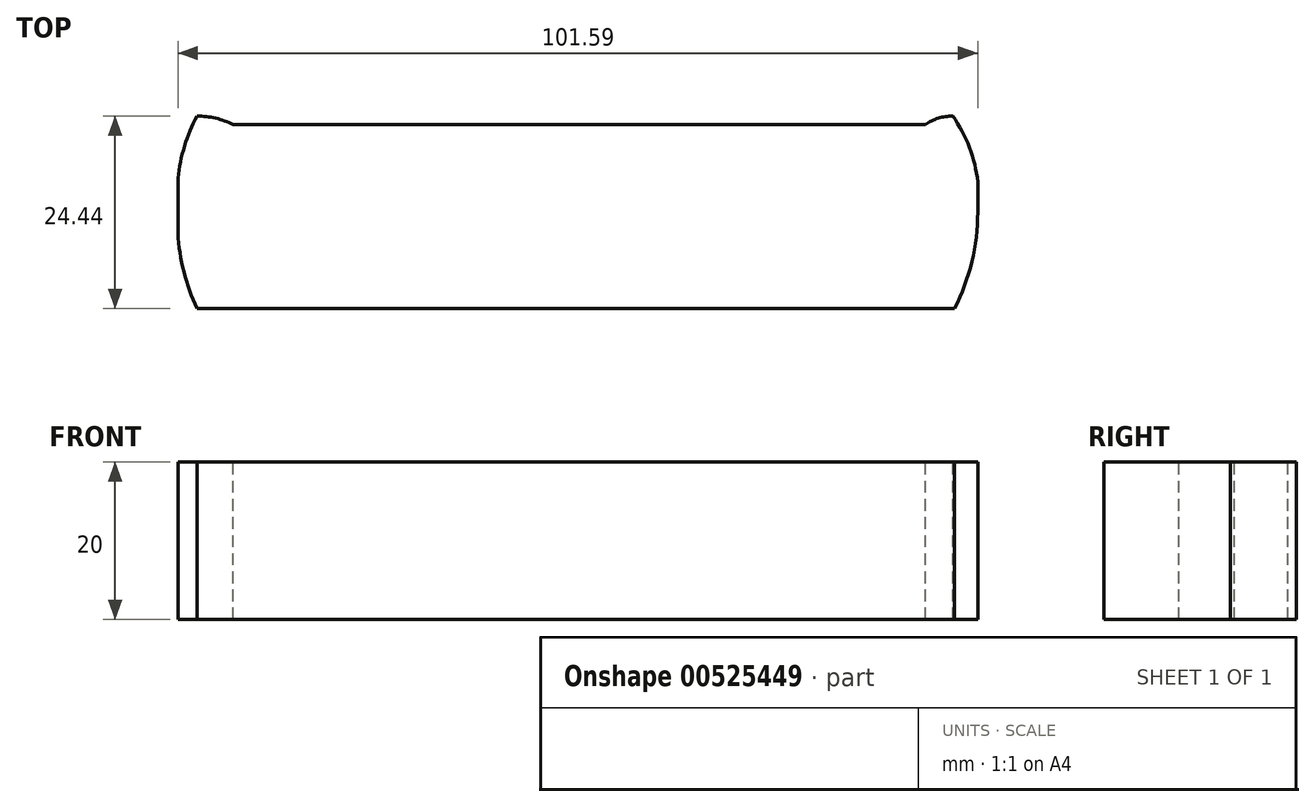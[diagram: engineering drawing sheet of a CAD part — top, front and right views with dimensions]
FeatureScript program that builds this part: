
annotation { "Feature Type Name" : "Feature", "Feature Type Description" : "" }
export const myFeature = defineFeature(function(context is Context, id is Id, definition is map)
    precondition{}
    {
        {
            var Q0;
            Q0=qCreatedBy(makeId("Top.planeOp"),FACE);
            var sketch = newSketch(context, id + "F0", { "sketchPlane" : qUnion([Q0])});
            skLineSegment(sketch, "E0.bottom", {"start": v(-50.41, 24.44) * mm, "end": v(51.18, 24.44) * mm});
            skLineSegment(sketch, "E0.top", {"start": v(-50.41, 0) * mm, "end": v(51.18, 0) * mm});
            skLineSegment(sketch, "E0.left", {"start": v(-50.41, 24.44) * mm, "end": v(-50.41, 0) * mm});
            skLineSegment(sketch, "E0.right", {"start": v(51.18, 24.44) * mm, "end": v(51.18, 0) * mm});
            skSolve(sketch);
        }
        {
            var Q0;
            Q0 = qSketchRegion(id + "F0", true);
            extrude(context, id + "F1", {"entities" : qUnion([Q0]), "depth" : 20 * mm, "offsetDistance" : 25 * mm});
        }
        {
            var Q0;
            Q0=makeQuery(id+"F1.opExtrude","CAP_FACE",FACE,{"disambiguationData":[OSD([sQuery(id+"F0.wireOp",EDGE,"E0.bottom"),sQuery(id+"F0.wireOp",EDGE,"E0.top"),sQuery(id+"F0.wireOp",EDGE,"E0.left"),sQuery(id+"F0.wireOp",EDGE,"E0.right")])],"isStart":false});
            var sketch = newSketch(context, id + "F2", { "sketchPlane" : qUnion([Q0])});
            skArc(sketch, "E1", {"start": v(-48, 24.44) * mm, "mid": v(-50.12, 18.51) * mm, "end": v(-50.41, 12.22) * mm});
            skArc(sketch, "E2", {"start": v(-50.41, 12.22) * mm, "mid": v(-49.97, 5.96) * mm, "end": v(-48, 0) * mm});
            skArc(sketch, "E3", {"start": v(51.18, 12.22) * mm, "mid": v(50.7, 18.62) * mm, "end": v(48, 24.44) * mm});
            skArc(sketch, "E4", {"start": v(48.22, 0) * mm, "mid": v(50.43, 5.93) * mm, "end": v(51.18, 12.22) * mm});
            skSolve(sketch);
        }
        {
            var Q0;
            {var subQ0=sQuery(id+"F2.wireOp",EDGE,"E1");var subQ1=makeQuery(id+"F1.opExtrude","CAP_EDGE",EDGE,{"disambiguationData":[OSD([sQuery(id+"F0.wireOp",EDGE,"E0.bottom")])],"isStart":false});var subQ2=makeQuery(id+"F2.imprint","INTERSECT",VERTEX,{"derivedFrom":[subQ1,subQ0]});Q0=makeQuery(id+"F2.imprint","IMPRINT",FACE,{"disambiguationData":[TD([[makeQuery(id+"F2.imprint","IMPRINT",EDGE,{"disambiguationData":[TD([[subQ2,-1.0]])],"derivedFrom":subQ0}),-1.0]])]});}
            var Q1;
            {var subQ0=sQuery(id+"F2.wireOp",EDGE,"E2");var subQ1=makeQuery(id+"F1.opExtrude","CAP_EDGE",EDGE,{"disambiguationData":[OSD([sQuery(id+"F0.wireOp",EDGE,"E0.top")])],"isStart":false});var subQ2=makeQuery(id+"F2.imprint","INTERSECT",VERTEX,{"derivedFrom":[subQ1,subQ0]});Q1=makeQuery(id+"F2.imprint","IMPRINT",FACE,{"disambiguationData":[TD([[makeQuery(id+"F2.imprint","IMPRINT",EDGE,{"disambiguationData":[TD([[subQ2,1.0]])],"derivedFrom":subQ0}),-1.0]])]});}
            var Q2;
            {var subQ0=sQuery(id+"F2.wireOp",EDGE,"E3");var subQ1=makeQuery(id+"F1.opExtrude","CAP_EDGE",EDGE,{"disambiguationData":[OSD([sQuery(id+"F0.wireOp",EDGE,"E0.bottom")])],"isStart":false});var subQ2=makeQuery(id+"F2.imprint","INTERSECT",VERTEX,{"derivedFrom":[subQ1,subQ0]});Q2=makeQuery(id+"F2.imprint","IMPRINT",FACE,{"disambiguationData":[TD([[makeQuery(id+"F2.imprint","IMPRINT",EDGE,{"disambiguationData":[TD([[subQ2,1.0]])],"derivedFrom":subQ0}),-1.0]])]});}
            var Q3;
            {var subQ0=sQuery(id+"F2.wireOp",EDGE,"E4");Q3=makeQuery(id+"F2.imprint","IMPRINT",FACE,{"disambiguationData":[TD([[makeQuery(id+"F2.imprint","IMPRINT",EDGE,{"derivedFrom":subQ0}),-1.0]])]});}
            extrude(context, id + "F3", {"entities" : qUnion([Q0, Q1, Q2, Q3]), "operationType" : NewBodyOperationType.REMOVE, "oppositeDirection" : true, "depth" : 25 * mm, "offsetDistance" : 25 * mm});
        }
        {
            var Q0;
            Q0=makeQuery(id+"F1.opExtrude","CAP_FACE",FACE,{"disambiguationData":[OSD([sQuery(id+"F0.wireOp",EDGE,"E0.bottom"),sQuery(id+"F0.wireOp",EDGE,"E0.top"),sQuery(id+"F0.wireOp",EDGE,"E0.left"),sQuery(id+"F0.wireOp",EDGE,"E0.right")])],"isStart":false});
            var sketch = newSketch(context, id + "F4", { "sketchPlane" : qUnion([Q0])});
            skArc(sketch, "E5", {"start": v(-43.4, 23.37) * mm, "mid": v(-45.64, 24.17) * mm, "end": v(-48, 24.44) * mm});
            skArc(sketch, "E6", {"start": v(48, 24.44) * mm, "mid": v(46.17, 24.17) * mm, "end": v(44.5, 23.37) * mm});
            skLineSegment(sketch, "E7", {"start": v(44.5, 23.37) * mm, "end": v(-43.4, 23.37) * mm});
            skSolve(sketch);
        }
        {
            var Q0;
            Q0=makeQuery(id+"F4.imprint","IMPRINT",FACE,{"disambiguationData":[TD([[makeQuery(id+"F4.imprint","IMPRINT",EDGE,{"derivedFrom":sQuery(id+"F4.wireOp",EDGE,"E5")}),-1.0]])]});
            extrude(context, id + "F5", {"entities" : qUnion([Q0]), "operationType" : NewBodyOperationType.REMOVE, "oppositeDirection" : true, "depth" : 25 * mm, "offsetDistance" : 25 * mm});
        }
    });
